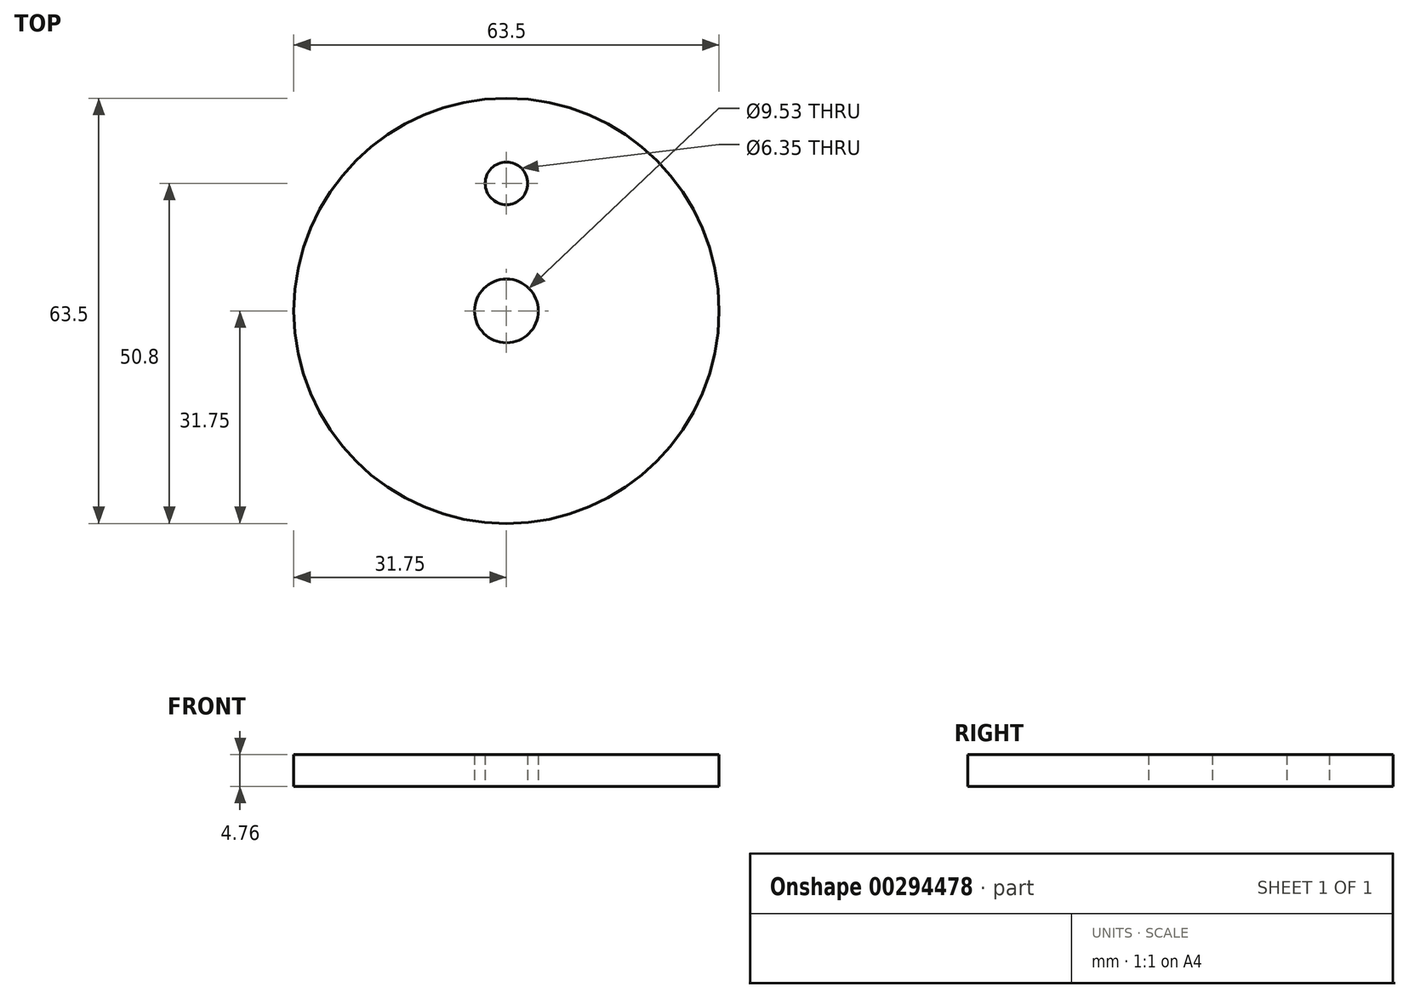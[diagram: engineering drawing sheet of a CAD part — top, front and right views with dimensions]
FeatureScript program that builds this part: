
annotation { "Feature Type Name" : "Feature", "Feature Type Description" : "" }
export const myFeature = defineFeature(function(context is Context, id is Id, definition is map)
    precondition{}
    {
        {
            var Q0;
            Q0=qCreatedBy(makeId("Top.planeOp"),FACE);
            var sketch = newSketch(context, id + "F0", { "sketchPlane" : qUnion([Q0])});
            skCircle(sketch, "E0", {"center": v(0, 0) * mm, "radius": 31.75 * mm});
            skCircle(sketch, "E1", {"center": v(0, 0) * mm, "radius": 4.76 * mm});
            skCircle(sketch, "E2", {"center": v(0, 19.05) * mm, "radius": 3.18 * mm});
            skCircle(sketch, "E3", {"center": v(0, 19.05) * mm, "radius": 9.53 * mm, "construction": true});
            skSolve(sketch);
        }
        {
            var Q0;
            Q0=makeQuery(id+"F0.imprint","IMPRINT",FACE,{"disambiguationData":[TD([[makeQuery(id+"F0.imprint","IMPRINT",EDGE,{"derivedFrom":sQuery(id+"F0.wireOp",EDGE,"E0")}),1.0]])]});
            extrude(context, id + "F1", {"entities" : qUnion([Q0]), "depth" : 4.76 * mm});
        }
    });
